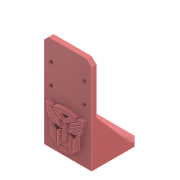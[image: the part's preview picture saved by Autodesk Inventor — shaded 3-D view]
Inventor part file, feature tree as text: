
AUTODESK INVENTOR PART (.ipt)
format: ipt  version: 2022 (Build 260153000, 153)  size: 574,464 bytes
history: native  units: mm
features: sketch x7, extrude x4, hole x2, other x2, rib x1, mirror x1, chamfer x1
ambient origin geometry x8: Origin, YZ Plane, XZ Plane, XY Plane, X Axis, Y Axis, Z Axis, Center Point
bodies: Solid1 (feature_tree)
feature tree (18):
  extrude  "Extrusion1"  Depth=30.0mm
  hole  "Hole1"  [1 undecoded]
  extrude  "Extrusion2"  Depth=4.0mm
  hole  "Hole2"  [1 undecoded]
  rib  "Rib1"
  mirror  "Mirror1"
  chamfer  "Chamfer1"  Distance=3.0mm
  extrude  "Decepticon Logo"  Depth=2.0mm
  extrude  "Autobots Logo"  Depth=2.0mm
  sketch  "Sketch1"  dims[d0=30.0mm d1=30.0mm]
  sketch  "Sketch2"  dims[d2=3.0mm d3=0.0mm d4=21.0mm]
  sketch  "Sketch5"  dims[d5=13.0mm d6=4.0mm]
  sketch  "Sketch6"  dims[d7=2.3mm d8=6.0mm d9=4.0mm d10=2.0mm d11=90.0deg d12=6.0mm d13=0.0mm d15=30.0mm]
  sketch  "Sketch7"  dims[d16=30.0mm]
  sketch  "Sketch8"  dims[d17=3.0mm]
  other  "Image1"
  sketch  "Sketch10"  dims[d18=3.0mm d19=3.0mm d20=0.0mm d21=15.0mm d22=13.5mm d23=7.0mm d24=3.2mm d25=6.0mm d26=4.0mm d27=2.0mm d28=90.0deg d29=6.0mm d30=0.0mm d31=22.0mm d35=1.0mm d36=2.0mm d37=0.0mm d38=0.0mm d39=1.0mm d40=1.0mm d41=27.0mm d42=32.0mm d43=3.0mm d44=2.0mm d45=45.0deg d71=2.0mm d72=0.0mm d75=5.5mm d157=2.0mm d158=0.0mm d73=0.5mm d74=0.872665mm]
  other  "Image2"
note: 2 required parameter values undecoded (feature->parameter linkage not recoverable at this tier; creation-order binding heuristic only, values carry confidence <= 0.55)
